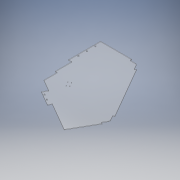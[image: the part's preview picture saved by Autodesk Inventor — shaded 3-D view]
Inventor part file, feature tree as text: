
AUTODESK INVENTOR PART (.ipt)
format: ipt  version: 2019.4 (Build 234330000, 330)  size: 236,032 bytes
history: native  units: mm
features: sketch x7, extrude x6, fillet x1
ambient origin geometry x8: Origin, YZ Plane, XZ Plane, XY Plane, X Axis, Y Axis, Z Axis, Center Point
bodies: Solid1 (feature_tree)
feature tree (14):
  extrude  "Extrusion1"  Depth=303.0mm
  extrude  "Extrusion2"  Depth=16.0mm
  extrude  "Extrusion3"  Depth=30.0mm TaperAngle=360.0deg
  extrude  "Extrusion4"  Depth=151.5mm
  extrude  "Extrusion5"  Depth=152.5mm
  sketch  "Sketch6"  dims[d14=17.0mm d15=3.0mm d16=0.0mm d17=35.0mm]
  extrude  "Extrusion6"  Depth=3.0mm TaperAngle=0.0deg
  fillet  "Fillet1"  Radius=35.0mm
  sketch  "Sketch1"  dims[d0=303.0mm d1=303.0mm]
  sketch  "Sketch2"  dims[d2=8.0mm d3=16.0mm]
  sketch  "Sketch3"  dims[d4=5.0mm d5=30.0mm d7=360.0deg]
  sketch  "Sketch4"  dims[d9=3.0mm d10=0.0mm d11=151.5mm]
  sketch  "Sketch5"  dims[d12=16.0mm d13=152.5mm]
  sketch  "Sketch7"  dims[d18=8.0mm d19=35.0mm d20=8.0mm d21=35.0mm d22=8.0mm d23=35.0mm d24=120.0deg d25=8.0mm d26=3.0mm d27=0.0mm d28=145.0mm d29=30.0deg d30=35.0mm d31=145.0mm d32=90.0deg d33=35.0mm d34=3.0mm d35=0.0mm d36=40.0mm d37=5.5mm d38=30.0mm d40=40.0mm d41=10.0mm d43=10.0mm d45=1.0mm d46=6.0mm d47=30.0mm d48=30.0mm d49=5.5mm d50=5.5mm d51=3.0mm d52=0.0mm d53=7.0mm d54=352.0mm d55=450.0mm d56=100.0mm d57=30.0deg d58=10.5mm d59=90.0deg d60=2.2mm d61=3.0mm d62=30.0deg d63=20.0mm d65=21.0mm d66=20.0mm d68=12.5mm d71=5.0mm d72=0.0mm d73=10.0mm]
